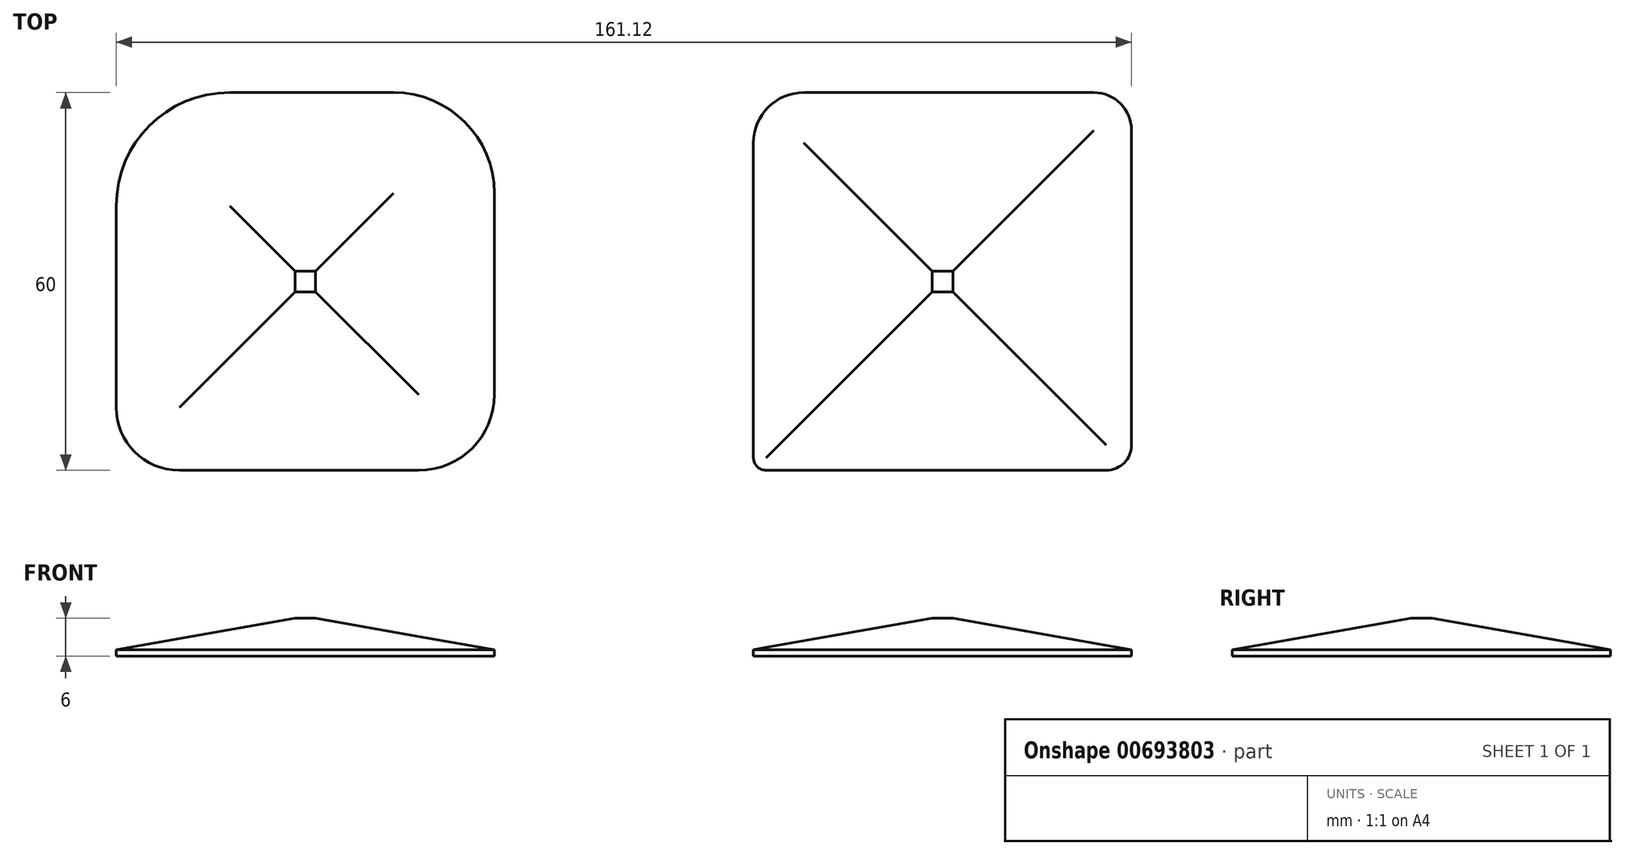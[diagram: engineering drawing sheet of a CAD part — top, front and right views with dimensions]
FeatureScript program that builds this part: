
annotation { "Feature Type Name" : "Feature", "Feature Type Description" : "" }
export const myFeature = defineFeature(function(context is Context, id is Id, definition is map)
    precondition{}
    {
        {
            var Q0;
            Q0=qCreatedBy(makeId("Top.planeOp"),FACE);
            var sketch = newSketch(context, id + "F0", { "sketchPlane" : qUnion([Q0])});
            skLineSegment(sketch, "E0.bottom", {"start": v(18, -30) * mm, "end": v(-20, -30) * mm});
            skLineSegment(sketch, "E0.top", {"start": v(14, 30) * mm, "end": v(-12, 30) * mm});
            skLineSegment(sketch, "E0.left", {"start": v(30, -18) * mm, "end": v(30, 14) * mm});
            skLineSegment(sketch, "E0.right", {"start": v(-30, -20) * mm, "end": v(-30, 12) * mm});
            skPoint(sketch, "E0.middle", {"position": v(0, 0) * mm});
            skPoint(sketch, "E1.visualSharp", {"position": v(-30, 30) * mm});
            skArc(sketch, "E1.filletArc", {"start": v(-12, 30) * mm, "mid": v(-24.73, 24.73) * mm, "end": v(-30, 12) * mm});
            skPoint(sketch, "E2.visualSharp", {"position": v(30, 30) * mm});
            skArc(sketch, "E2.filletArc", {"start": v(30, 14) * mm, "mid": v(25.31, 25.31) * mm, "end": v(14, 30) * mm});
            skPoint(sketch, "E3.visualSharp", {"position": v(30, -30) * mm});
            skArc(sketch, "E3.filletArc", {"start": v(18, -30) * mm, "mid": v(26.49, -26.49) * mm, "end": v(30, -18) * mm});
            skPoint(sketch, "E4.visualSharp", {"position": v(-30, -30) * mm});
            skArc(sketch, "E4.filletArc", {"start": v(-30, -20) * mm, "mid": v(-27.07, -27.07) * mm, "end": v(-20, -30) * mm});
            skLineSegment(sketch, "E5.bottom", {"start": v(73.12, -30) * mm, "end": v(127.12, -30) * mm});
            skLineSegment(sketch, "E5.top", {"start": v(79.12, 30) * mm, "end": v(125.12, 30) * mm});
            skLineSegment(sketch, "E5.left", {"start": v(71.12, -28) * mm, "end": v(71.12, 22) * mm});
            skLineSegment(sketch, "E5.right", {"start": v(131.12, -26) * mm, "end": v(131.12, 24) * mm});
            skPoint(sketch, "E5.middle", {"position": v(101.12, 0) * mm});
            skPoint(sketch, "E6.visualSharp", {"position": v(71.12, 30) * mm});
            skArc(sketch, "E6.filletArc", {"start": v(79.12, 30) * mm, "mid": v(73.46, 27.66) * mm, "end": v(71.12, 22) * mm});
            skPoint(sketch, "E7.visualSharp", {"position": v(131.12, 30) * mm});
            skArc(sketch, "E7.filletArc", {"start": v(131.12, 24) * mm, "mid": v(129.36, 28.24) * mm, "end": v(125.12, 30) * mm});
            skPoint(sketch, "E8.visualSharp", {"position": v(131.12, -30) * mm});
            skArc(sketch, "E8.filletArc", {"start": v(127.12, -30) * mm, "mid": v(129.94, -28.83) * mm, "end": v(131.12, -26) * mm});
            skPoint(sketch, "E9.visualSharp", {"position": v(71.12, -30) * mm});
            skArc(sketch, "E9.filletArc", {"start": v(71.12, -28) * mm, "mid": v(71.7, -29.41) * mm, "end": v(73.12, -30) * mm});
            skSolve(sketch);
        }
        {
            var Q0;
            Q0=makeQuery(id+"F0.imprint","IMPRINT",FACE,{"disambiguationData":[TD([[makeQuery(id+"F0.imprint","IMPRINT",EDGE,{"derivedFrom":sQuery(id+"F0.wireOp",EDGE,"E0.bottom")}),-1.0]])]});
            extrude(context, id + "F1", {"entities" : qUnion([Q0]), "depth" : 5 * mm, "offsetDistance" : 25 * mm, "hasDraft" : true, "draftAngle" : 80 * degree, "draftPullDirection" : true});
        }
        {
            var Q0;
            Q0=makeQuery(id+"F0.imprint","IMPRINT",FACE,{"disambiguationData":[TD([[makeQuery(id+"F0.imprint","IMPRINT",EDGE,{"derivedFrom":sQuery(id+"F0.wireOp",EDGE,"E5.bottom")}),1.0]])]});
            extrude(context, id + "F2", {"entities" : qUnion([Q0]), "depth" : 5 * mm, "offsetDistance" : 25 * mm, "hasDraft" : true, "draftAngle" : 80 * degree, "draftPullDirection" : true});
        }
        {
            var Q0;
            Q0=makeQuery(id+"F1.opExtrude","CAP_FACE",FACE,{"disambiguationData":[OSD([sQuery(id+"F0.wireOp",EDGE,"E0.bottom"),sQuery(id+"F0.wireOp",EDGE,"E0.top"),sQuery(id+"F0.wireOp",EDGE,"E0.left"),sQuery(id+"F0.wireOp",EDGE,"E0.right"),sQuery(id+"F0.wireOp",EDGE,"E1.filletArc"),sQuery(id+"F0.wireOp",EDGE,"E2.filletArc"),sQuery(id+"F0.wireOp",EDGE,"E3.filletArc"),sQuery(id+"F0.wireOp",EDGE,"E4.filletArc")])],"isStart":true});
            var Q1;
            Q1=makeQuery(id+"F2.opExtrude","CAP_FACE",FACE,{"disambiguationData":[OSD([sQuery(id+"F0.wireOp",EDGE,"E5.bottom"),sQuery(id+"F0.wireOp",EDGE,"E5.top"),sQuery(id+"F0.wireOp",EDGE,"E5.left"),sQuery(id+"F0.wireOp",EDGE,"E5.right"),sQuery(id+"F0.wireOp",EDGE,"E6.filletArc"),sQuery(id+"F0.wireOp",EDGE,"E7.filletArc"),sQuery(id+"F0.wireOp",EDGE,"E8.filletArc"),sQuery(id+"F0.wireOp",EDGE,"E9.filletArc")])],"isStart":true});
            extrude(context, id + "F3", {"entities" : qUnion([Q0, Q1]), "operationType" : NewBodyOperationType.ADD, "depth" : 1 * mm, "offsetDistance" : 25 * mm});
        }
    });
